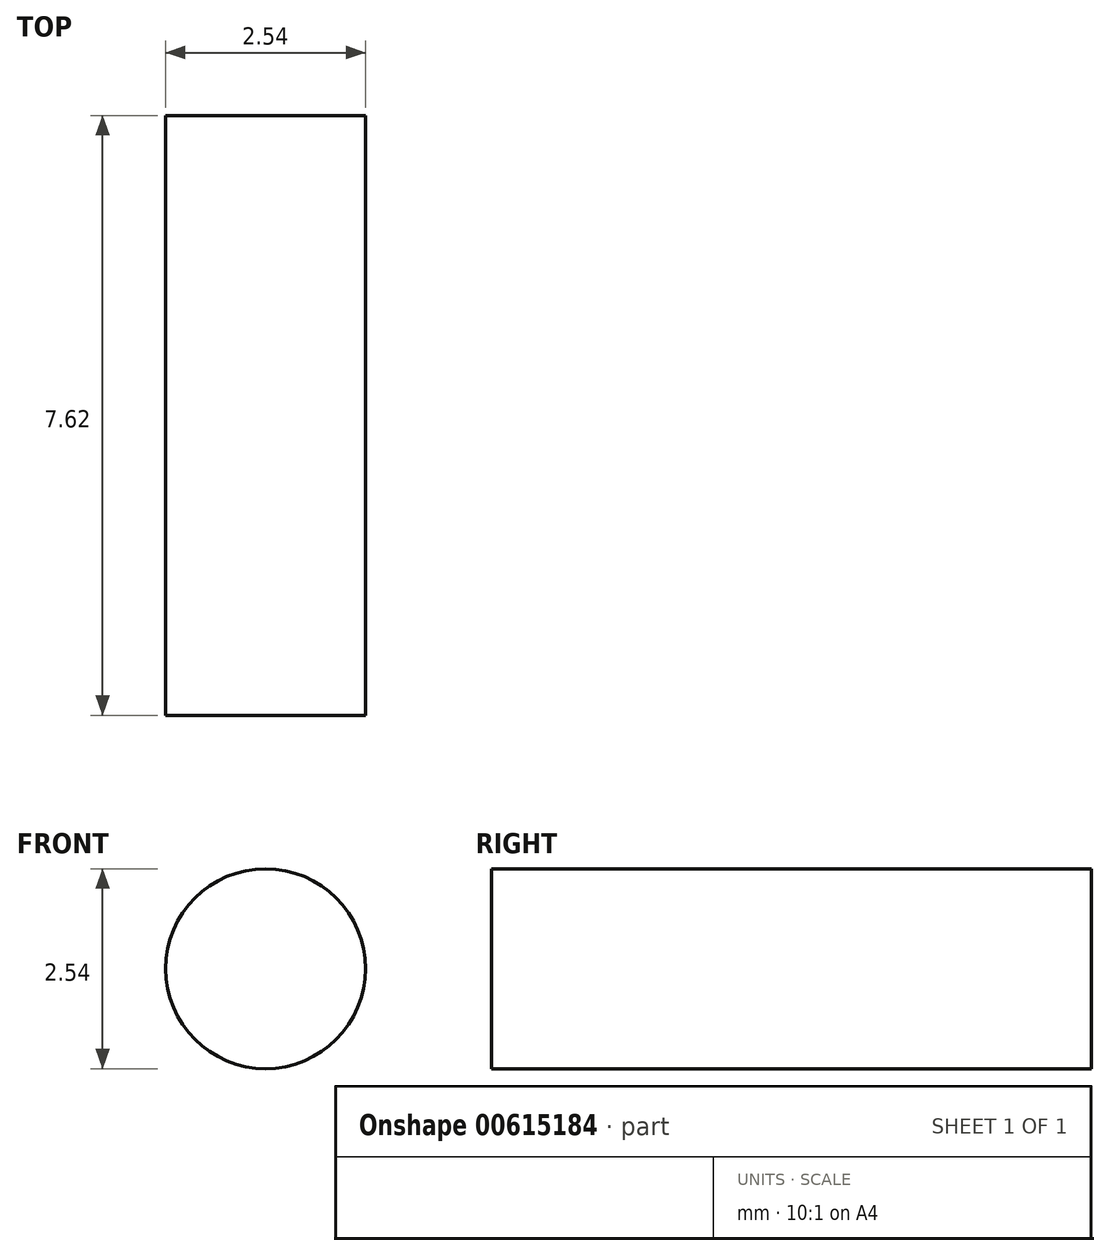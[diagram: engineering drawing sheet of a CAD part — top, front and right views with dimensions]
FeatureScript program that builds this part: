
annotation { "Feature Type Name" : "Feature", "Feature Type Description" : "" }
export const myFeature = defineFeature(function(context is Context, id is Id, definition is map)
    precondition{}
    {
        {
            var Q0;
            Q0=qCreatedBy(makeId("Front.planeOp"),FACE);
            var sketch = newSketch(context, id + "F0", { "sketchPlane" : qUnion([Q0])});
            skCircle(sketch, "E0", {"center": v(0, 0) * mm, "radius": 1.27 * mm});
            skSolve(sketch);
        }
        {
            var Q0;
            Q0 = qSketchRegion(id + "F0", true);
            extrude(context, id + "F1", {"entities" : qUnion([Q0]), "depth" : 7.62 * mm, "offsetDistance" : 25.4 * mm});
        }
    });
